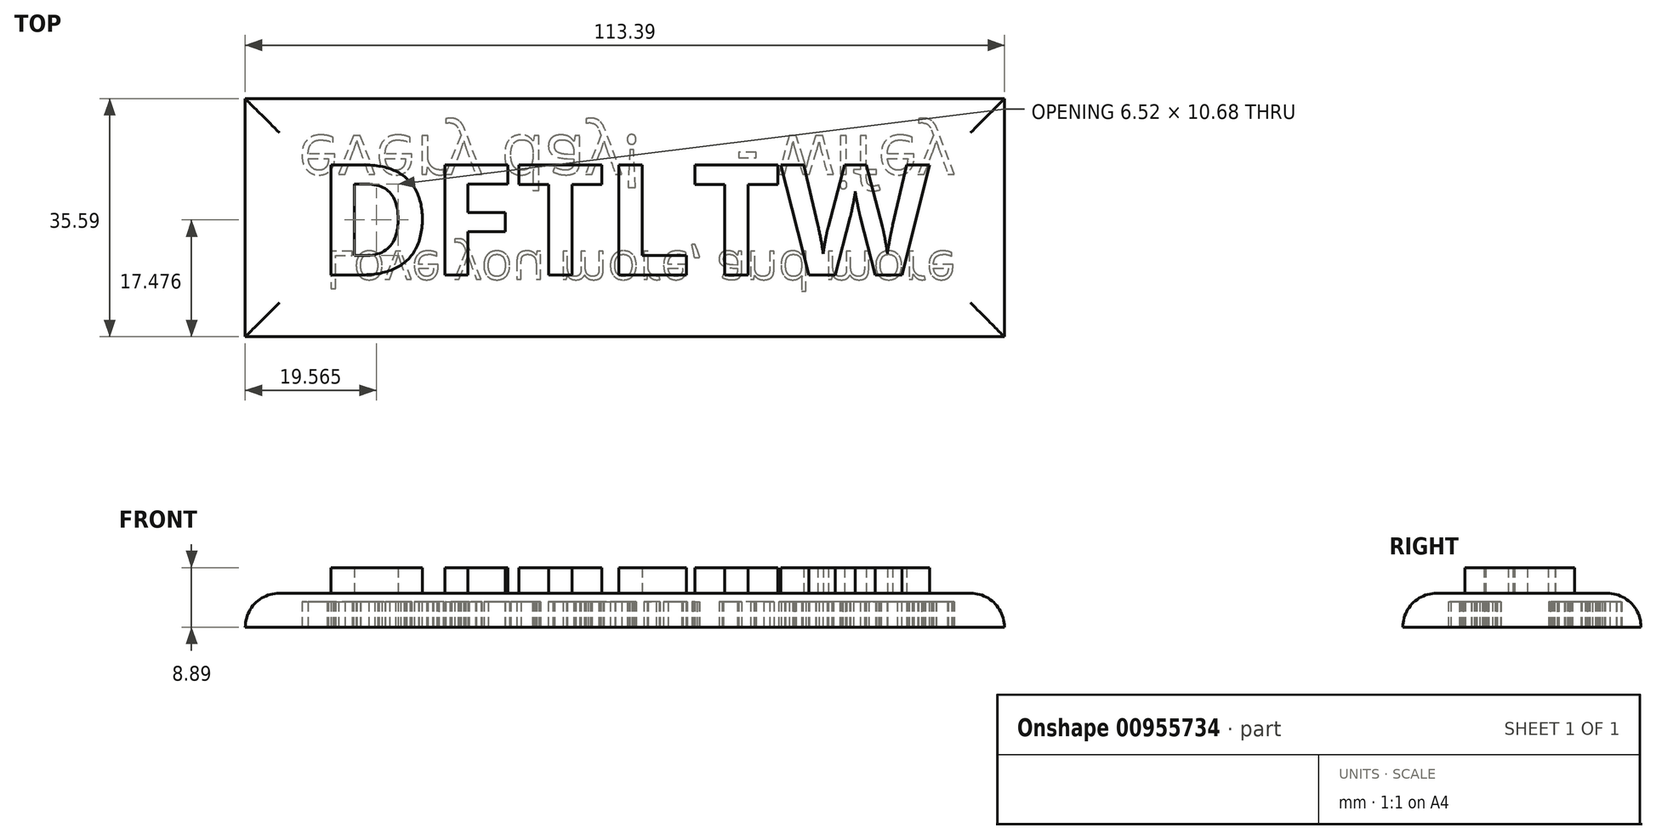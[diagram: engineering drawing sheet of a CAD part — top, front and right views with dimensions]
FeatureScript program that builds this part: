
annotation { "Feature Type Name" : "Feature", "Feature Type Description" : "" }
export const myFeature = defineFeature(function(context is Context, id is Id, definition is map)
    precondition{}
    {
        {
            var Q0;
            Q0=qCreatedBy(makeId("Top.planeOp"),FACE);
            var sketch = newSketch(context, id + "F0", { "sketchPlane" : qUnion([Q0])});
            skText(sketch, "E0", { "text": "DFTLTW", "fontName": "OpenSans-Bold.ttf"});
            const initialGuessF0  = {"E0": [-0.0467, -0.00742, 1, 0, 0.01655]};
            skSetInitialGuess(sketch, initialGuessF0);
            skSolve(sketch);
        }
        {
            var Q0;
            Q0 = qSketchRegion(id + "F0", true);
            extrude(context, id + "F1", {"entities" : qUnion([Q0]), "depth" : 3.8 * mm, "offsetDistance" : 25.4 * mm});
        }
        {
            var Q0;
            Q0=qCreatedBy(makeId("Top.planeOp"),FACE);
            var sketch = newSketch(context, id + "F2", { "sketchPlane" : qUnion([Q0])});
            skLineSegment(sketch, "E1.bottom", {"start": v(-57.46, 18.91) * mm, "end": v(55.93, 18.91) * mm});
            skLineSegment(sketch, "E1.top", {"start": v(-57.46, -16.68) * mm, "end": v(55.93, -16.68) * mm});
            skLineSegment(sketch, "E1.left", {"start": v(-57.46, 18.91) * mm, "end": v(-57.46, -16.68) * mm});
            skLineSegment(sketch, "E1.right", {"start": v(55.93, 18.91) * mm, "end": v(55.93, -16.68) * mm});
            skSolve(sketch);
        }
        {
            var Q0;
            Q0 = qSketchRegion(id + "F2", true);
            extrude(context, id + "F3", {"entities" : qUnion([Q0]), "oppositeDirection" : true, "depth" : 5.08 * mm, "offsetDistance" : 25.4 * mm});
        }
        {
            var Q0;
            Q0=makeQuery(id+"F3.opExtrude","CAP_EDGE",EDGE,{"disambiguationData":[OSD([sQuery(id+"F2.wireOp",EDGE,"E1.bottom")])],"isStart":true});
            var Q1;
            Q1=makeQuery(id+"F3.opExtrude","CAP_EDGE",EDGE,{"disambiguationData":[OSD([sQuery(id+"F2.wireOp",EDGE,"E1.left")])],"isStart":true});
            var Q2;
            Q2=makeQuery(id+"F3.opExtrude","CAP_EDGE",EDGE,{"disambiguationData":[OSD([sQuery(id+"F2.wireOp",EDGE,"E1.top")])],"isStart":true});
            var Q3;
            Q3=makeQuery(id+"F3.opExtrude","CAP_EDGE",EDGE,{"disambiguationData":[OSD([sQuery(id+"F2.wireOp",EDGE,"E1.right")])],"isStart":true});
            fillet(context, id + "F4", {"entities" : qUnion([Q0, Q1, Q2, Q3]), "radius" : 5.08 * mm, "tangentPropagation" : true, "allowEdgeOverflow" : false});
        }
        {
            var Q0;
            Q0=makeQuery(id+"F3.opExtrude","CAP_FACE",FACE,{"disambiguationData":[OSD([sQuery(id+"F2.wireOp",EDGE,"E1.bottom"),sQuery(id+"F2.wireOp",EDGE,"E1.top"),sQuery(id+"F2.wireOp",EDGE,"E1.left"),sQuery(id+"F2.wireOp",EDGE,"E1.right")])],"isStart":false});
            var sketch = newSketch(context, id + "F5", { "sketchPlane" : qUnion([Q0])});
            skText(sketch, "E2", { "text": "Love you more, and more", "fontName": "OpenSans-Regular.ttf"});
            const initialGuessF5  = {"E2": [-0.0454, 0.0039, 1, 0, 0.00565]};
            skSetInitialGuess(sketch, initialGuessF5);
            skSolve(sketch);
        }
        {
            var Q0;
            Q0=makeQuery(id+"F5.imprint","IMPRINT",FACE,{"disambiguationData":[TD([[makeQuery(id+"F5.imprint","IMPRINT",EDGE,{"derivedFrom":sQuery(id+"F5.wireOp",EDGE,"E2.sketch_text.stroke-0")}),1.0]])]});
            var sketch = newSketch(context, id + "F6", { "sketchPlane" : qUnion([Q0])});
            skText(sketch, "E3", { "text": "every day!     - wifey", "fontName": "OpenSans-Regular.ttf"});
            const initialGuessF6  = {"E3": [-0.0496, -0.0134, 1, 0, 0.0078]};
            skSetInitialGuess(sketch, initialGuessF6);
            skSolve(sketch);
        }
        {
            var Q0;
            Q0 = qSketchRegion(id + "F5", true);
            extrude(context, id + "F7", {"entities" : qUnion([Q0]), "operationType" : NewBodyOperationType.REMOVE, "oppositeDirection" : true, "depth" : 3.8 * mm, "offsetDistance" : 25.4 * mm});
        }
        {
            var Q0;
            Q0 = qSketchRegion(id + "F6", true);
            var Q1;
            Q1 = qSketchRegion(id + "F5", true);
            extrude(context, id + "F8", {"entities" : qUnion([Q0, Q1]), "operationType" : NewBodyOperationType.REMOVE, "oppositeDirection" : true, "depth" : 3.8 * mm, "offsetDistance" : 25.4 * mm});
        }
    });
